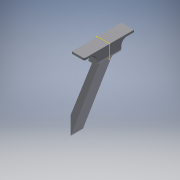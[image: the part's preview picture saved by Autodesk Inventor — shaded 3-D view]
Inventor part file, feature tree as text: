
AUTODESK INVENTOR PART (.ipt)
format: ipt  version: 2018 (Build 220112000, 112)  size: 202,240 bytes
history: native  units: in
note: dims shown in document units (in); Inventor stores cm internally (conversion verified against a paired STEP export)
features: extrude x8, sketch x7, plane x3, fillet x3
ambient origin geometry x8: Origin, YZ Plane, XZ Plane, XY Plane, X Axis, Y Axis, Z Axis, Center Point
bodies: Solid1 (feature_tree)
feature tree (21):
  extrude  "Extrusion1"  Depth=0.6in
  plane  "Work Plane1"
  plane  "Work Plane2"
  plane  "Work Plane3"
  extrude  "Extrusion4"  Depth=0.3in TaperAngle=0.0deg
  extrude  "Extrusion5"  Depth=1.0in TaperAngle=0.0deg
  extrude  "Extrusion7"  Depth=0.3in
  extrude  "Extrusion8"  Depth=0.3in
  extrude  "Extrusion9"  Depth=0.125in
  fillet  "Fillet3"  Radius=0.125in
  fillet  "Fillet4"  Radius=1000.0in
  extrude  "Extrusion11"  Depth=0.0394in
  extrude  "Extrusion12"  [1 undecoded]
  fillet  "Fillet5"  [1 undecoded]
  sketch  "Sketch1"  dims[d0=0.3in d1=0.6in]
  sketch  "Sketch3"  dims[d2=0.3in d3=0.0in d8=0.3in d9=0.0in]
  sketch  "Sketch4"  dims[d10=1.0in d11=0.0in d14=1.0in d15=0.0in]
  sketch  "Sketch7"  dims[d16=1.0in d17=0.0in d18=0.3in]
  sketch  "Sketch8"  dims[d19=0.3in d20=0.3in]
  sketch  "Sketch10"  dims[d21=0.05in d22=0.0in d27=0.125in d28=0.125in d29=1000.0in d30=0.0in]
  sketch  "Sketch11"  dims[d31=1000.0in d32=0.0in d33=0.0394in]
note: 2 required parameter values undecoded (feature->parameter linkage not recoverable at this tier; creation-order binding heuristic only, values carry confidence <= 0.55)
